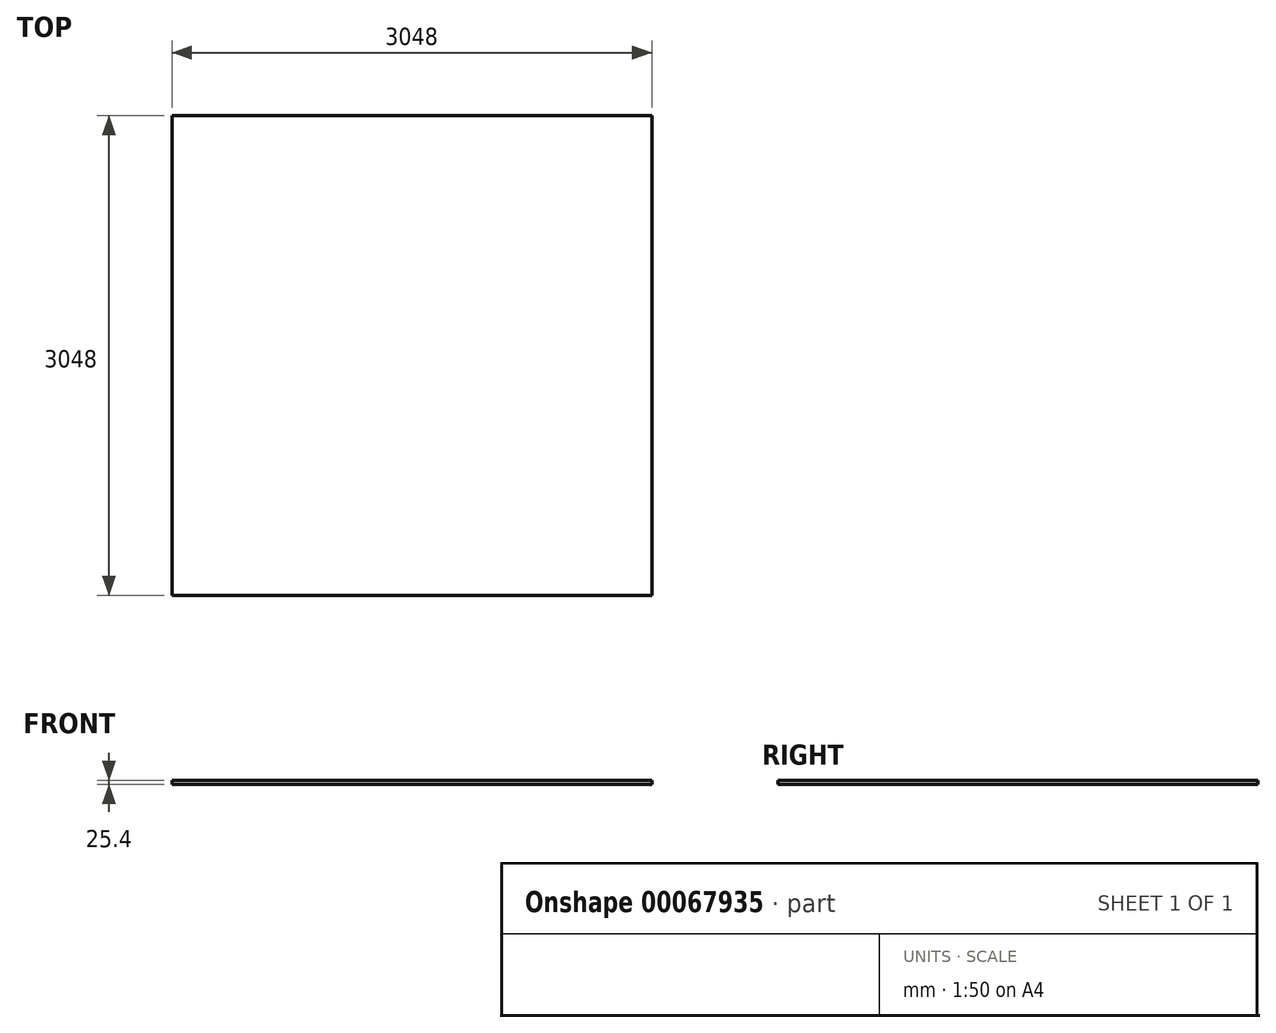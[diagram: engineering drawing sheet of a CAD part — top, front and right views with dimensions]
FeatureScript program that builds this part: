
annotation { "Feature Type Name" : "Feature", "Feature Type Description" : "" }
export const myFeature = defineFeature(function(context is Context, id is Id, definition is map)
    precondition{}
    {
        {
            var Q0;
            Q0=qCreatedBy(makeId("Top.planeOp"),FACE);
            var sketch = newSketch(context, id + "F0", { "sketchPlane" : qUnion([Q0])});
            skLineSegment(sketch, "E0.bottom", {"start": v(-1532.78, 1572.79) * mm, "end": v(1515.22, 1572.79) * mm});
            skLineSegment(sketch, "E0.top", {"start": v(-1532.78, -1475.21) * mm, "end": v(1515.22, -1475.21) * mm});
            skLineSegment(sketch, "E0.left", {"start": v(-1532.78, 1572.79) * mm, "end": v(-1532.78, -1475.21) * mm});
            skLineSegment(sketch, "E0.right", {"start": v(1515.22, 1572.79) * mm, "end": v(1515.22, -1475.21) * mm});
            skSolve(sketch);
        }
        {
            var Q0;
            Q0 = qSketchRegion(id + "F0", true);
            extrude(context, id + "F1", {"entities" : qUnion([Q0]), "depth" : 25.4 * mm});
        }
    });
